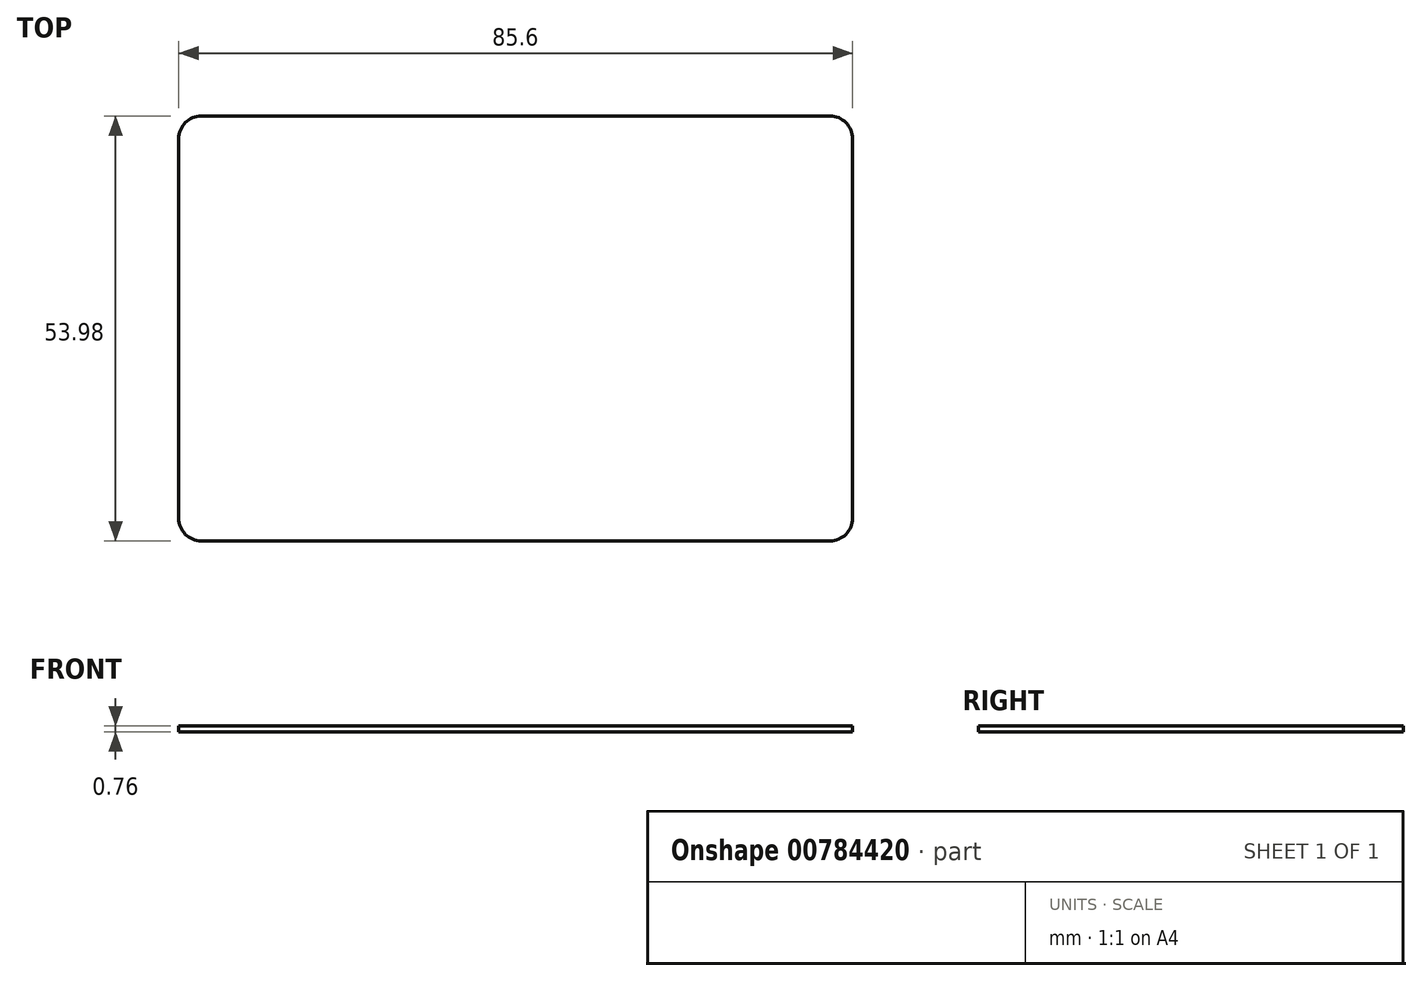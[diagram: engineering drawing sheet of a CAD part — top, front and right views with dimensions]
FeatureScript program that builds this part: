
annotation { "Feature Type Name" : "Feature", "Feature Type Description" : "" }
export const myFeature = defineFeature(function(context is Context, id is Id, definition is map)
    precondition{}
    {
        {
            var Q0;
            Q0=qCreatedBy(makeId("Top.planeOp"),FACE);
            var sketch = newSketch(context, id + "F0", { "sketchPlane" : qUnion([Q0])});
            skLineSegment(sketch, "E0.bottom", {"start": v(39.92, 26.99) * mm, "end": v(-39.92, 27) * mm});
            skLineSegment(sketch, "E0.top", {"start": v(39.92, -27) * mm, "end": v(-39.92, -26.99) * mm});
            skLineSegment(sketch, "E0.left", {"start": v(42.8, 24.1) * mm, "end": v(42.8, -24.11) * mm});
            skLineSegment(sketch, "E0.right", {"start": v(-42.8, 24.1) * mm, "end": v(-42.8, -24.1) * mm});
            skPoint(sketch, "E0.middle", {"position": v(0, 0) * mm});
            skPoint(sketch, "E1.visualSharp", {"position": v(-42.8, 27) * mm});
            skArc(sketch, "E1.filletArc", {"start": v(-39.92, 27) * mm, "mid": v(-41.96, 26.15) * mm, "end": v(-42.8, 24.11) * mm});
            skPoint(sketch, "E2.visualSharp", {"position": v(-42.8, -26.99) * mm});
            skArc(sketch, "E2.filletArc", {"start": v(-42.8, -24.1) * mm, "mid": v(-41.96, -26.15) * mm, "end": v(-39.92, -26.99) * mm});
            skPoint(sketch, "E3.visualSharp", {"position": v(42.8, -27) * mm});
            skArc(sketch, "E3.filletArc", {"start": v(39.92, -27) * mm, "mid": v(41.96, -26.15) * mm, "end": v(42.8, -24.11) * mm});
            skPoint(sketch, "E4.visualSharp", {"position": v(42.8, 26.99) * mm});
            skArc(sketch, "E4.filletArc", {"start": v(42.8, 24.1) * mm, "mid": v(41.96, 26.15) * mm, "end": v(39.92, 26.99) * mm});
            skSolve(sketch);
        }
        {
            var Q0;
            Q0=makeQuery(id+"F0.imprint","IMPRINT",FACE,{"disambiguationData":[TD([[makeQuery(id+"F0.imprint","IMPRINT",EDGE,{"derivedFrom":sQuery(id+"F0.wireOp",EDGE,"E0.bottom")}),1.0]])]});
            extrude(context, id + "F1", {"entities" : qUnion([Q0]), "depth" : 0.76 * mm, "offsetDistance" : 25 * mm});
        }
    });
